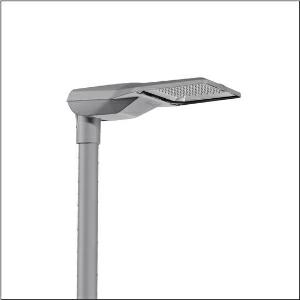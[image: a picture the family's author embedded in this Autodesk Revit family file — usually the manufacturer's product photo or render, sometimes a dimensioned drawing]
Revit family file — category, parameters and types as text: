
# Revit family: streetlight_sl_21_iq_midi___st1_0a_5xe3d21d08nb_d513
name_source: partatom
category: Lighting Fixtures
units: mm (PartAtom-declared; Revit-internal decimal feet)

## family parameters
Cut with Voids When Loaded = No
Host = Face
Light Source = No
Part Type = Normal
Room Calculation Point = No
Round Connector Dimension = Use Diameter
Shared = No

## types (1)
- --- (1 x LED, 19210 lm, 155.5 W, 2200K)
    Apparent Load = 155 VA
    CIE Flux Codes = 40 73 97 100 100
    Color Rendering = 70
    Color Temperature = 2200K
    Default Elevation = 1800 mm
    Description = Streetlight SL 21 iQ midi, mast luminaire, primary light control with lens, of PMMA, primary optical cover: cover, of toughened safety glass, transparent, light distribution: ST1.0a, light emission: direct distribution, primary light characteristic: asymmetric, installation type: post-top, side-entry, LED, High Power LED, rated luminous flux: 19.210lm, luminous efficacy: 124lm/W, light colour: 722, colour temperature: 2200K, control: Auto-Match, Temp-Guard, Lumen-Switch, Night-Set, Smart-Wire, Light-Fading, Desk-Remote (wireless, voltage-free reading and setting of iQ features in the workshop via application-optimized NFC function/RFID function), optimised constant luminous flux control (CLO 2.0), presetting dimming linear, mains connection: 230..240V, AC, 50/60Hz, start of lifetime: 156W, end of service life: 162W, reduction: 69W, luminaire housing, of diecast aluminium, powder-coated, Siteco® metallic grey (DB 702S), corrosivity category C5 mid according to DIN EN ISO 12944, please order mast flange separately, inclination adjustable: 0°, 5°, 10°, 15°, sealing non-destructively replaceable, multi-level sealing system, length: 644mm, width: 335mm, height: 110mm, mast flange for spigot size: 42mm (side-entry): 5XC10008XM4, 60/48mm (side-entry/post-top): 5XC10108XM2, 76/60mm (side-entry/post-top): 5XC10108XM1, protection rating (complete): IP66, insulation class (complete): insulation class II (safety insulation), certification: CE, ENEC, ENEC+, VDE, impact resistance: IK09, permissible operating ambient temperature for outdoor applications: -40..+50°C, standard-compliant lighting for roads and squares, packaging unit: 1 piece

Light Distribution: ST1.0a
    Height = 111 mm
    Lamp = 1 x LED
    Lamp Light Flux = 19210 lm
    Lamp Power = 155.5 W
    Lamp count = 1
    Length = 644 mm
    Luminous efficacy = 124 lm/W
    Manufacturer = Siteco
    ModVariant = No
    Model = 5XE3D21D08NB
    Number of Poles = 1
    OnlyDefault = Yes
    Power Factor = 1
    Product Name = Streetlight SL 21 iQ midi | ST1.0a
    Product group = mast luminaire | pylon top
    ProductGroupID = 6100
    Protection Class = Protection class II
    Protection Degree = IP 66
    RLX_Detail_Level = 1
    RLX_Emergency_Light_Flux = 0 lm
    RLX_Emergency_Type = 0
    RLX_Emergency_Type_DB = No
    RlxData = <blob elided: 91533 chars, md5=218b3771>
    Socket = socket
    Standby Power = 0 W
    System Light Flux = 19210 lm
    System Power = 155 W
    Type Comments = factory setting: luminous flux: 100 % | dim-lin: 254 | 823 mA
    Type Image = l_1004298.jpg
    URL = http://relux.com
    VarID = @adj_121555
    Voltage = 0 V
    Weight = 0.00 kg
    Width = 336 mm

## geometry (parser evidence)
native form markers: Blend x4, Sweep x12
no freeform markers — native parametric forms only
